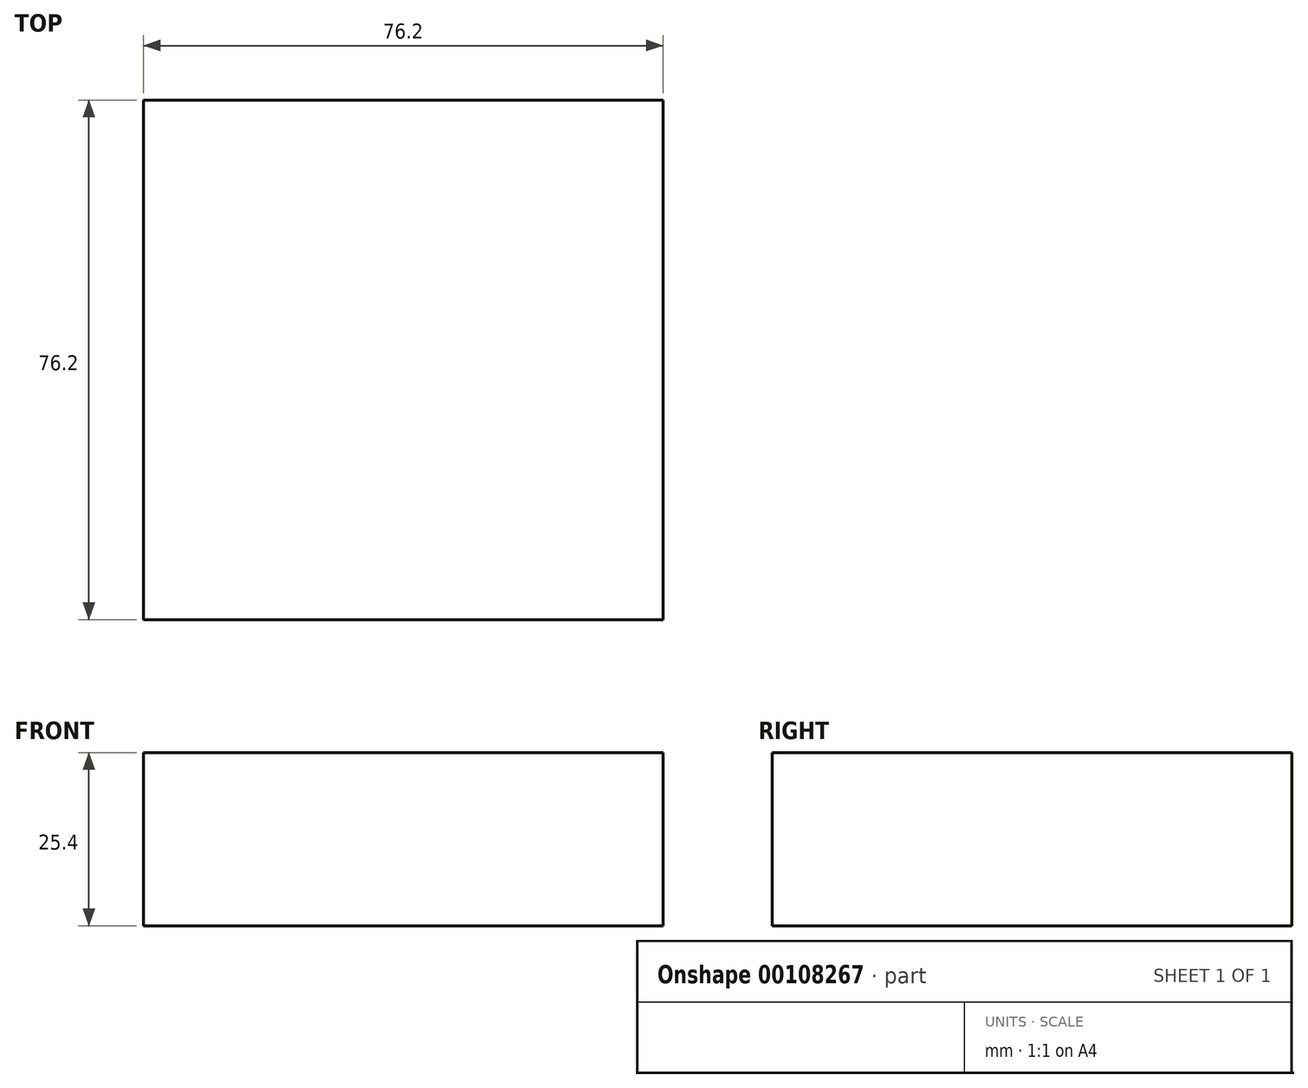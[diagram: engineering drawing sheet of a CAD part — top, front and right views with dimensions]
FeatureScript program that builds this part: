
annotation { "Feature Type Name" : "Feature", "Feature Type Description" : "" }
export const myFeature = defineFeature(function(context is Context, id is Id, definition is map)
    precondition{}
    {
        {
            var Q0;
            Q0=qCreatedBy(makeId("Top.planeOp"),FACE);
            var sketch = newSketch(context, id + "F0", { "sketchPlane" : qUnion([Q0])});
            skLineSegment(sketch, "E0.bottom", {"start": v(0, 0) * mm, "end": v(76.2, 0) * mm});
            skLineSegment(sketch, "E0.top", {"start": v(0, -76.2) * mm, "end": v(76.2, -76.2) * mm});
            skLineSegment(sketch, "E0.left", {"start": v(0, 0) * mm, "end": v(0, -76.2) * mm});
            skLineSegment(sketch, "E0.right", {"start": v(76.2, 0) * mm, "end": v(76.2, -76.2) * mm});
            skSolve(sketch);
        }
        {
            var Q0;
            Q0 = qSketchRegion(id + "F0", true);
            extrude(context, id + "F1", {"entities" : qUnion([Q0]), "offsetDistance" : 25.4 * mm, "depth" : 25.4 * mm});
        }
    });
